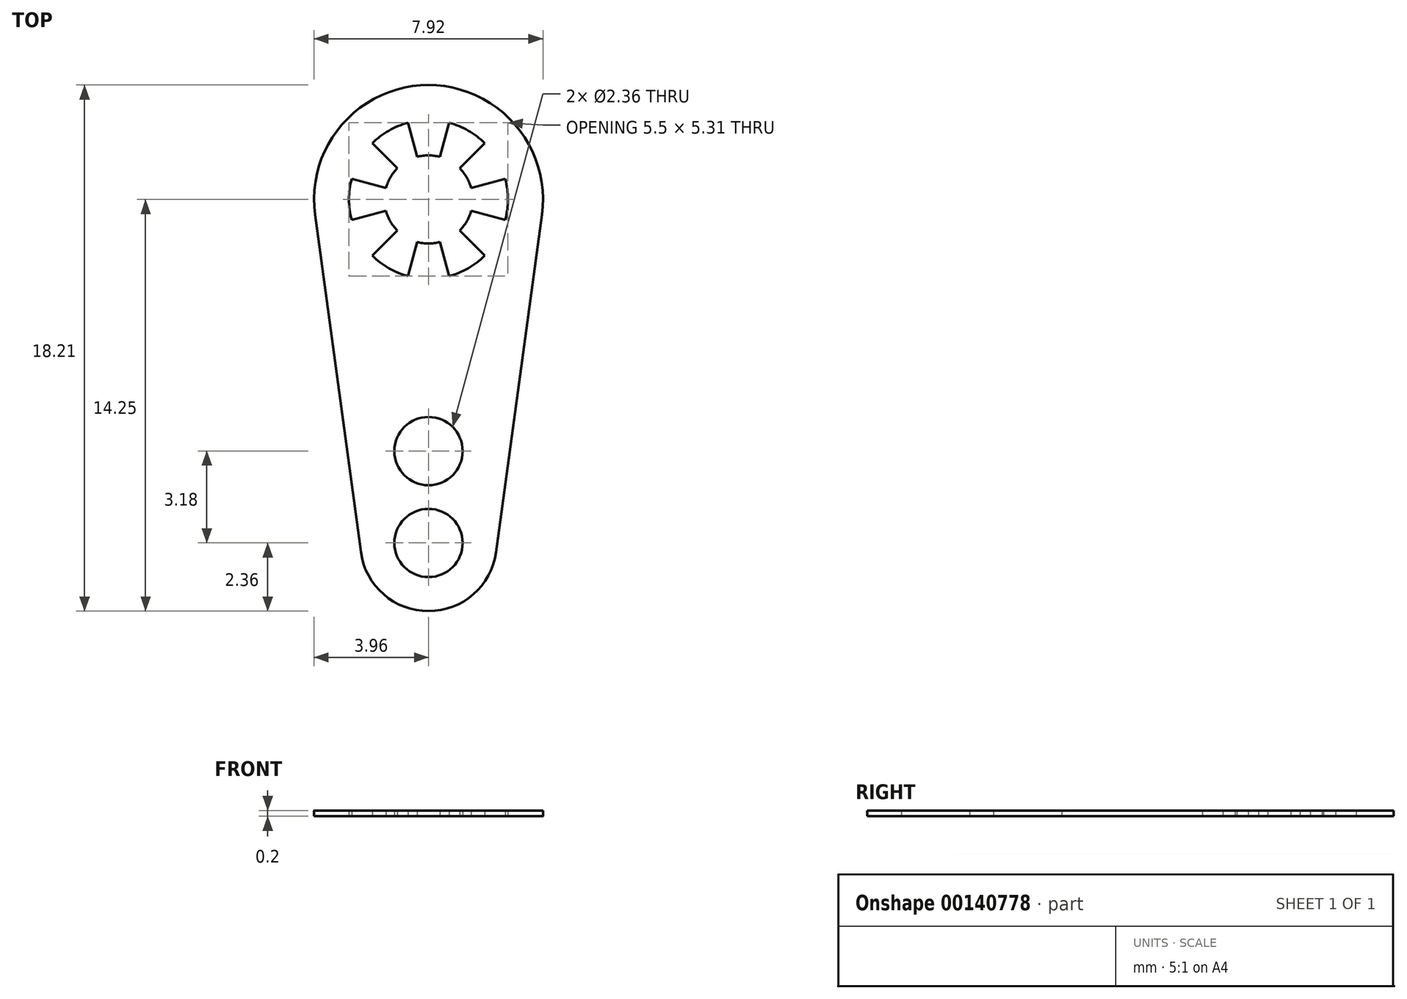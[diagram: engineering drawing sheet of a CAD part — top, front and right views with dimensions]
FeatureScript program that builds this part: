
annotation { "Feature Type Name" : "Feature", "Feature Type Description" : "" }
export const myFeature = defineFeature(function(context is Context, id is Id, definition is map)
    precondition{}
    {
        {
            var Q0;
            Q0=qCreatedBy(makeId("Top.planeOp"),FACE);
            var sketch = newSketch(context, id + "F0", { "sketchPlane" : qUnion([Q0])});
            skArc(sketch, "E0", {"start": v(-1.47, -0.4) * mm, "mid": v(-1.32, -0.76) * mm, "end": v(-1.08, -1.08) * mm});
            skArc(sketch, "E1", {"start": v(3.92, -0.53) * mm, "mid": v(0, 3.96) * mm, "end": v(-3.92, -0.53) * mm});
            skArc(sketch, "E2", {"start": v(-2.34, -12.2) * mm, "mid": v(0, -14.25) * mm, "end": v(2.34, -12.2) * mm});
            skCircle(sketch, "E3", {"center": v(0, -11.9) * mm, "radius": 1.18 * mm});
            skCircle(sketch, "E4", {"center": v(0, -8.71) * mm, "radius": 1.18 * mm});
            skLineSegment(sketch, "E5", {"start": v(-3.92, -0.53) * mm, "end": v(-2.34, -12.2) * mm});
            skLineSegment(sketch, "E6", {"start": v(2.34, -12.2) * mm, "end": v(3.92, -0.53) * mm});
            skArc(sketch, "E7", {"start": v(-2.66, 0.71) * mm, "mid": v(-2.75, 0) * mm, "end": v(-2.66, -0.71) * mm});
            skLineSegment(sketch, "E8", {"start": v(-1.47, 0.4) * mm, "end": v(-2.66, 0.71) * mm});
            skLineSegment(sketch, "E9", {"start": v(-1.47, -0.4) * mm, "end": v(-2.66, -0.71) * mm});
            skLineSegment(sketch, "E10", {"start": v(-2.66, 0.71) * mm, "end": v(-2.66, -0.71) * mm, "construction": true});
            skLineSegment(sketch, "E11.1.0", {"start": v(-1.08, -1.08) * mm, "end": v(-1.94, -1.94) * mm});
            skLineSegment(sketch, "E11.1.1", {"start": v(-0.4, -1.47) * mm, "end": v(-0.71, -2.66) * mm});
            skLineSegment(sketch, "E11.2.0", {"start": v(0.4, -1.47) * mm, "end": v(0.71, -2.66) * mm});
            skLineSegment(sketch, "E11.2.1", {"start": v(1.08, -1.08) * mm, "end": v(1.94, -1.94) * mm});
            skLineSegment(sketch, "E11.3.0", {"start": v(1.47, -0.4) * mm, "end": v(2.66, -0.71) * mm});
            skLineSegment(sketch, "E11.3.1", {"start": v(1.47, 0.4) * mm, "end": v(2.66, 0.71) * mm});
            skLineSegment(sketch, "E11.4.0", {"start": v(1.08, 1.08) * mm, "end": v(1.94, 1.94) * mm});
            skLineSegment(sketch, "E11.4.1", {"start": v(0.4, 1.47) * mm, "end": v(0.71, 2.66) * mm});
            skLineSegment(sketch, "E11.5.0", {"start": v(-0.4, 1.47) * mm, "end": v(-0.71, 2.66) * mm});
            skLineSegment(sketch, "E11.5.1", {"start": v(-1.08, 1.08) * mm, "end": v(-1.94, 1.94) * mm});
            skArc(sketch, "E12.trimOffspring", {"start": v(-1.08, 1.08) * mm, "mid": v(-1.32, 0.76) * mm, "end": v(-1.47, 0.4) * mm});
            skArc(sketch, "E13.trimOffspring", {"start": v(-0.71, 2.66) * mm, "mid": v(-1.37, 2.38) * mm, "end": v(-1.94, 1.94) * mm});
            skArc(sketch, "E14.trimOffspring", {"start": v(0.4, 1.47) * mm, "mid": v(0, 1.52) * mm, "end": v(-0.4, 1.47) * mm});
            skArc(sketch, "E15.trimOffspring", {"start": v(1.94, 1.94) * mm, "mid": v(1.38, 2.38) * mm, "end": v(0.71, 2.66) * mm});
            skArc(sketch, "E16.trimOffspring", {"start": v(1.47, 0.4) * mm, "mid": v(1.32, 0.76) * mm, "end": v(1.08, 1.08) * mm});
            skArc(sketch, "E17.trimOffspring", {"start": v(2.66, -0.71) * mm, "mid": v(2.75, 0) * mm, "end": v(2.66, 0.71) * mm});
            skArc(sketch, "E18.trimOffspring", {"start": v(1.08, -1.08) * mm, "mid": v(1.32, -0.76) * mm, "end": v(1.47, -0.4) * mm});
            skArc(sketch, "E19.trimOffspring", {"start": v(0.71, -2.66) * mm, "mid": v(1.37, -2.38) * mm, "end": v(1.94, -1.94) * mm});
            skArc(sketch, "E20.trimOffspring", {"start": v(-0.4, -1.47) * mm, "mid": v(0, -1.52) * mm, "end": v(0.4, -1.47) * mm});
            skArc(sketch, "E21.trimOffspring", {"start": v(-1.94, -1.94) * mm, "mid": v(-1.38, -2.38) * mm, "end": v(-0.71, -2.66) * mm});
            skSolve(sketch);
        }
        {
            var Q0;
            Q0 = qSketchRegion(id + "F0", true);
            extrude(context, id + "F1", {"entities" : qUnion([Q0]), "depth" : 0.2 * mm});
        }
    });
